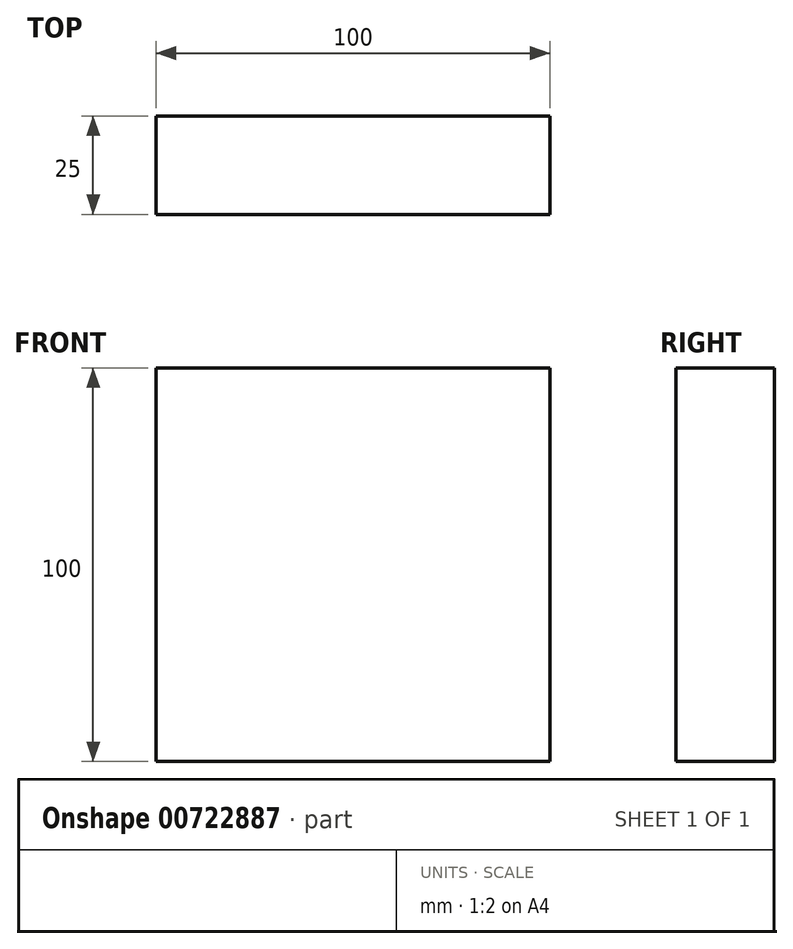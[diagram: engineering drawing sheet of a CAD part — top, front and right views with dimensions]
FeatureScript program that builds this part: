
annotation { "Feature Type Name" : "Feature", "Feature Type Description" : "" }
export const myFeature = defineFeature(function(context is Context, id is Id, definition is map)
    precondition{}
    {
        {
            var Q0;
            Q0=qCreatedBy(makeId("Front.planeOp"),FACE);
            var sketch = newSketch(context, id + "F0", { "sketchPlane" : qUnion([Q0])});
            skLineSegment(sketch, "E0.bottom", {"start": v(-57.02, 47.07) * mm, "end": v(42.98, 47.07) * mm});
            skLineSegment(sketch, "E0.top", {"start": v(-57.02, -52.93) * mm, "end": v(42.98, -52.93) * mm});
            skLineSegment(sketch, "E0.left", {"start": v(-57.02, 47.07) * mm, "end": v(-57.02, -52.93) * mm});
            skLineSegment(sketch, "E0.right", {"start": v(42.98, 47.07) * mm, "end": v(42.98, -52.93) * mm});
            skSolve(sketch);
        }
        {
            var Q0;
            Q0=makeQuery(id+"F0.imprint","IMPRINT",FACE,{"disambiguationData":[TD([[makeQuery(id+"F0.imprint","IMPRINT",EDGE,{"derivedFrom":sQuery(id+"F0.wireOp",EDGE,"E0.bottom")}),-1.0]])]});
            extrude(context, id + "F1", {"entities" : qUnion([Q0]), "depth" : 25 * mm, "offsetDistance" : 25 * mm});
        }
    });
